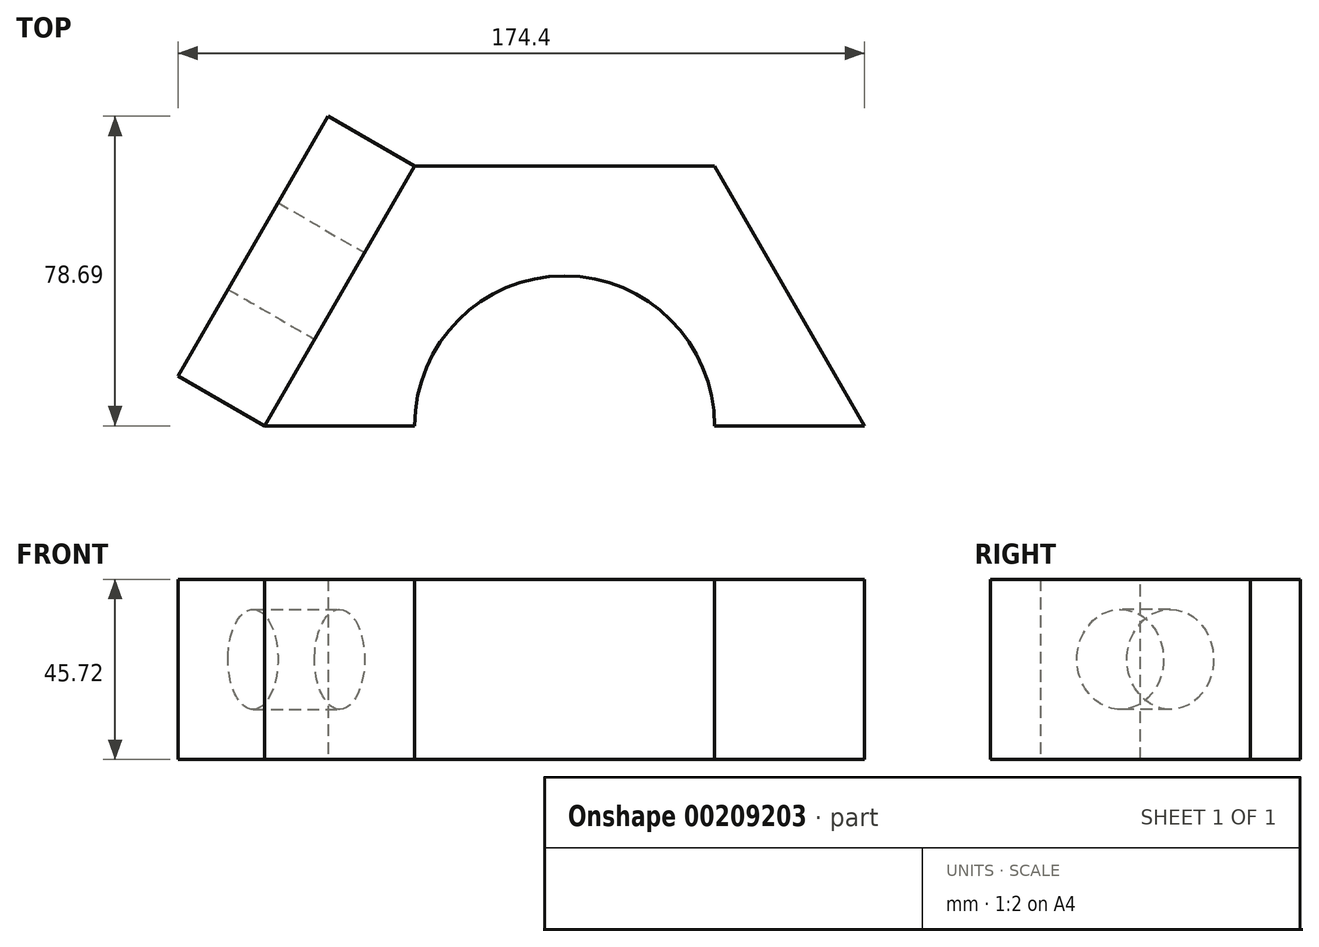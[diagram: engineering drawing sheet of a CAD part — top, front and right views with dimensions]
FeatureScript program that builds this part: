
annotation { "Feature Type Name" : "Feature", "Feature Type Description" : "" }
export const myFeature = defineFeature(function(context is Context, id is Id, definition is map)
    precondition{}
    {
        {
            var Q0;
            Q0=qCreatedBy(makeId("Top.planeOp"),FACE);
            var sketch = newSketch(context, id + "F0", { "sketchPlane" : qUnion([Q0])});
            skLineSegment(sketch, "E0.bottom", {"start": v(0, 0) * mm, "end": v(76.2, 0) * mm});
            skLineSegment(sketch, "E0.top", {"start": v(-38.1, 66) * mm, "end": v(38.1, 66) * mm});
            skLineSegment(sketch, "E0.left", {"start": v(0, 0) * mm, "end": v(-38.1, 66) * mm});
            skLineSegment(sketch, "E0.right", {"start": v(76.2, 0) * mm, "end": v(38.1, 66) * mm});
            skLineSegment(sketch, "E1", {"start": v(-38.1, 66) * mm, "end": v(-76.2, 0) * mm});
            skLineSegment(sketch, "E2", {"start": v(-76.2, 0) * mm, "end": v(0, 0) * mm});
            skSolve(sketch);
        }
        {
            var Q0;
            Q0=makeQuery(id+"F0.imprint","IMPRINT",FACE,{"disambiguationData":[TD([[makeQuery(id+"F0.imprint","IMPRINT",EDGE,{"derivedFrom":sQuery(id+"F0.wireOp",EDGE,"E0.left")}),1.0]])]});
            var Q1;
            Q1=makeQuery(id+"F0.imprint","IMPRINT",FACE,{"disambiguationData":[TD([[makeQuery(id+"F0.imprint","IMPRINT",EDGE,{"derivedFrom":sQuery(id+"F0.wireOp",EDGE,"E0.bottom")}),1.0]])]});
            extrude(context, id + "F1", {"entities" : qUnion([Q0, Q1]), "depth" : 45.72 * mm});
        }
        {
            var Q0;
            Q0=makeQuery(id+"F1.opExtrude","CAP_FACE",FACE,{"disambiguationData":[OSD([sQuery(id+"F0.wireOp",EDGE,"E0.bottom"),sQuery(id+"F0.wireOp",EDGE,"E0.top"),sQuery(id+"F0.wireOp",EDGE,"E0.right"),sQuery(id+"F0.wireOp",EDGE,"E1"),sQuery(id+"F0.wireOp",EDGE,"E2")])],"isStart":false});
            var sketch = newSketch(context, id + "F2", { "sketchPlane" : qUnion([Q0])});
            skCircle(sketch, "E3", {"center": v(0, 0) * mm, "radius": 38.1 * mm});
            skSolve(sketch);
        }
        {
            var Q0;
            Q0 = qSketchRegion(id + "F2", true);
            extrude(context, id + "F3", {"entities" : qUnion([Q0]), "operationType" : NewBodyOperationType.REMOVE, "endBound" : BoundingType.THROUGH_ALL, "oppositeDirection" : true, "depth" : 25.4 * mm});
        }
        {
            var Q0;
            Q0=makeQuery(id+"F1.opExtrude","SWEPT_FACE",FACE,{"disambiguationData":[OSD([sQuery(id+"F0.wireOp",EDGE,"E1")])]});
            var sketch = newSketch(context, id + "F4", { "sketchPlane" : qUnion([Q0])});
            skCircle(sketch, "E4", {"center": v(0, 25.4) * mm, "radius": 12.7 * mm});
            skPoint(sketch, "E4.centerSnap0", {"position": v(0, 0) * mm});
            skSolve(sketch);
        }
        {
            var Q0;
            Q0=makeQuery(id+"F4.imprint","IMPRINT",FACE,{"disambiguationData":[TD([[makeQuery(id+"F4.imprint","IMPRINT",EDGE,{"derivedFrom":sQuery(id+"F4.wireOp",EDGE,"E4")}),-1.0]])]});
            extrude(context, id + "F5", {"entities" : qUnion([Q0]), "depth" : 25.4 * mm});
        }
    });
